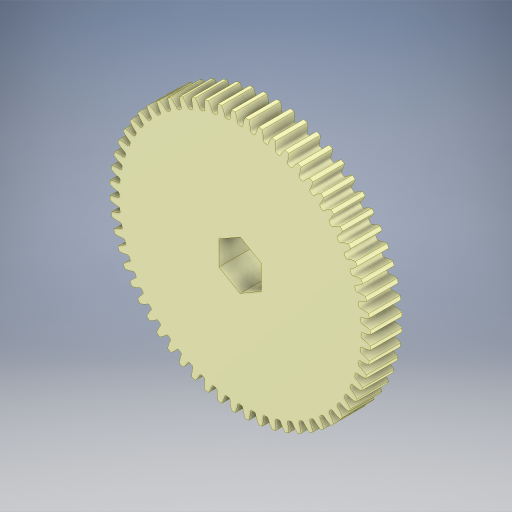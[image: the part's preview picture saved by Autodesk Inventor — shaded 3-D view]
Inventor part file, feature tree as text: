
AUTODESK INVENTOR PART (.ipt)
format: ipt  version: 2024 (Build 280153000, 153)  size: 1,088,512 bytes
history: native  units: in
note: dims shown in document units (in); Inventor stores cm internally (conversion verified against a paired STEP export)
features: extrude x2, sketch x2, boolean_combine x1
ambient origin geometry x8: Origin, YZ Plane, XZ Plane, XY Plane, X Axis, Y Axis, Z Axis, Center Point
bodies: Solid1 (feature_tree)
feature tree (5):
  extrude  "Extrusion1"  Depth=1.0in TaperAngle=0.0deg
  extrude  "Extrusion2"  [1 undecoded]
  sketch  "Sketch1"  dims[d0=1.0in d1=0.0in d2=1.0in d3=0.0in]
  sketch  "Sketch2"
  boolean_combine  "Combine1"
note: 1 required parameter value undecoded (feature->parameter linkage not recoverable at this tier; creation-order binding heuristic only, values carry confidence <= 0.55)
